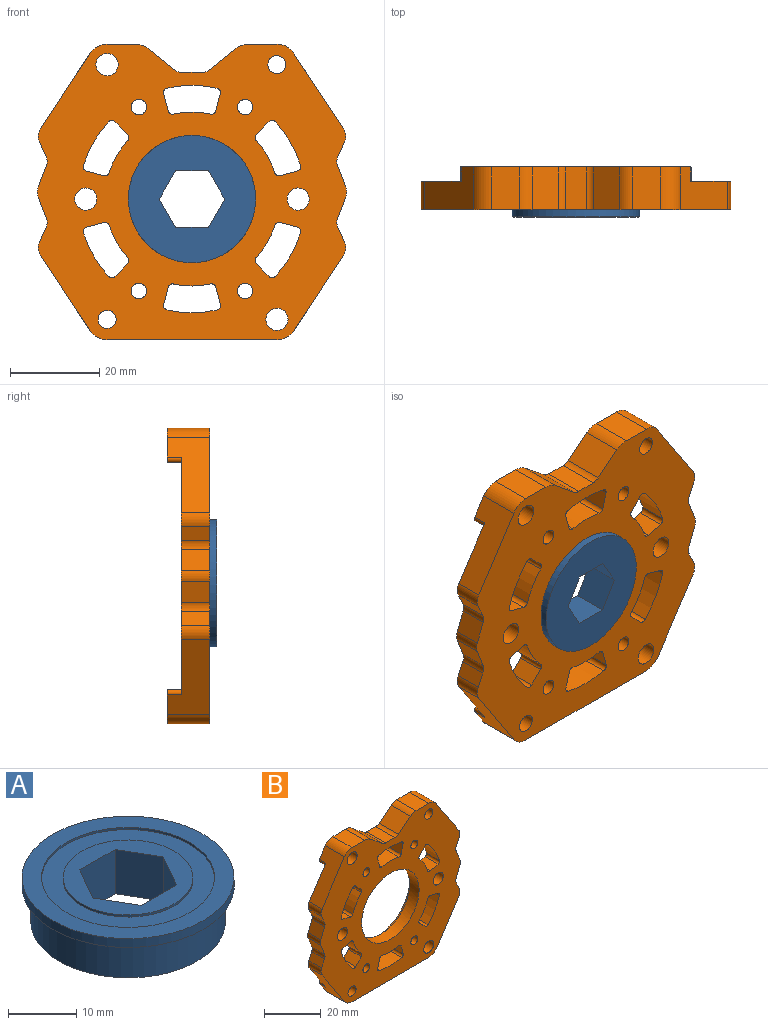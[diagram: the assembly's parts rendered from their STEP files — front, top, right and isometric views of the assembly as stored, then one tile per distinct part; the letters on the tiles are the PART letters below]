
ASSEMBLY  parts=2 mates=1
PART A: 15 faces, bbox 31.1x31.1x7.9 mm
  f0: cylinder r=12.7mm len=25.4mm, axis (0,0,1), area 30.4mm2, adj f7,f8
  f1: cylinder r=15.56mm len=31.12mm, axis (0,0,1), area 155.2mm2, adj f6,f7
  f2: cylinder r=14.27mm len=28.55mm, axis (0,0,1), area 569.5mm2, adj f5,f6
  f3: cylinder r=9.53mm len=19.05mm, axis (0,0,1), area 22.8mm2, adj f4,f8
  f4: plane 19.05x19.05mm, normal (0,0,1), area 144.9mm2, adj f3,f9,f10,f11,f12,f13,f14
  f5: plane 28.55x28.55mm, normal (0,0,-1), area 500mm2, adj f2,f9,f10,f11,f12,f13,f14
  f6: plane 31.12x31.12mm, normal (0,0,-1), area 120.2mm2, adj f1,f2
  f7: plane 31.12x31.12mm, normal (0,0,1), area 253.7mm2, adj f0,f1
  f8: plane 25.4x25.4mm, normal (0,0,1), area 221.7mm2, adj f0,f3
  f9: plane 7.94x6.36mm, normal (-0.87,-0.5,0), area 58.3mm2, adj f4,f5,f10,f14
  f10: plane 7.94x6.36mm, normal (-0.87,0.5,0), area 58.3mm2, adj f4,f5,f9,f11
  f11: plane 7.94x7.34mm, normal (0,1,0), area 58.3mm2, adj f4,f5,f10,f12
  f12: plane 7.94x6.36mm, normal (0.87,0.5,0), area 58.3mm2, adj f4,f5,f11,f13
  f13: plane 7.94x6.36mm, normal (0.87,-0.5,0), area 58.3mm2, adj f4,f5,f12,f14
  f14: plane 7.94x7.34mm, normal (0,-1,0), area 58.3mm2, adj f4,f5,f9,f13
PART B: 111 faces, bbox 69.4x9.5x66.3 mm
  f0: cylinder r=15.88mm len=31.75mm, axis (0,1,0), area 164.7mm2, adj f97,f110
  f1: cylinder r=2.54mm len=6.35mm, axis (0,-1,0), area 12.9mm2, adj f35,f36,f50,f97
  f2: cylinder r=2.54mm len=6.35mm, axis (0,1,0), area 12.9mm2, adj f44,f45,f50,f97
  f3: cylinder r=2.49mm len=6.35mm, axis (0,-1,0), area 99.3mm2, adj f50,f97
  f4: cylinder r=2.49mm len=6.35mm, axis (0,-1,0), area 99.3mm2, adj f50,f97
  f5: cylinder r=0.79mm len=3.18mm, axis (0,-1,0), area 5.3mm2, adj f25,f43,f96,f97,f102
  f6: cylinder r=0.79mm len=3.18mm, axis (0,1,0), area 5.3mm2, adj f25,f39,f95,f97,f101
  f7: cylinder r=2.02mm len=9.53mm, axis (0,-1,0), area 120.8mm2, adj f50,f51
  f8: cylinder r=2.02mm len=9.53mm, axis (0,-1,0), area 120.8mm2, adj f25,f50
  f9: cylinder r=3.17mm len=6.35mm, axis (0,1,0), area 14.8mm2, adj f36,f37,f50,f97
  f10: cylinder r=3.17mm len=6.35mm, axis (0,-1,0), area 20.5mm2, adj f47,f48,f50,f97
  f11: cylinder r=3.17mm len=6.35mm, axis (0,-1,0), area 20.4mm2, adj f43,f44,f50,f97
  f12: cylinder r=1mm len=6.35mm, axis (0,-1,0), area 9.7mm2, adj f50,f87,f93,f97
  f13: cylinder r=1mm len=9.53mm, axis (0,-1,0), area 14.5mm2, adj f25,f50,f82,f83,f96,f97,f102
  f14: cylinder r=1mm len=6.35mm, axis (0,-1,0), area 10.2mm2, adj f50,f73,f79,f97
  f15: cylinder r=1mm len=6.35mm, axis (0,-1,0), area 10.2mm2, adj f50,f66,f67,f97
  f16: cylinder r=1mm len=6.35mm, axis (0,-1,0), area 10.2mm2, adj f50,f59,f60,f97
  f17: cylinder r=1mm len=6.35mm, axis (0,-1,0), area 9.7mm2, adj f50,f52,f58,f97
  f18: cylinder r=1.73mm len=6.35mm, axis (0,-1,0), area 68.9mm2, adj f50,f97
  f19: cylinder r=1.73mm len=6.35mm, axis (0,-1,0), area 68.9mm2, adj f50,f97
  f20: cylinder r=1.73mm len=6.35mm, axis (0,-1,0), area 68.9mm2, adj f50,f97
  f21: cylinder r=1.73mm len=6.35mm, axis (0,-1,0), area 68.9mm2, adj f50,f97
  f22: cylinder r=2.49mm len=9.53mm, axis (0,1,0), area 149mm2, adj f50,f51
  f23: cylinder r=2.49mm len=9.53mm, axis (0,1,0), area 149mm2, adj f25,f50
  f24: cylinder r=14.27mm len=28.55mm, axis (0,1,0), area 421.5mm2, adj f50,f110
  f25: plane 51.79x7.45mm, normal (0,1,0), area 308.4mm2, adj f5,f6,f8,f13,f23,f39,f40,f41
  f26: plane 9.53x6.35mm, normal (0,0,1), area 60.5mm2, adj f27,f49,f50,f51
  f27: cylinder r=4.58mm len=9.53mm, axis (0,1,0), area 29.5mm2, adj f26,f28,f50,f51
  f28: plane 9.53x5.96mm, normal (-0.63,0,0.78), area 72.8mm2, adj f27,f50,f51,f106
  f29: plane 9.53x4.56mm, normal (0,0,1), area 43.5mm2, adj f50,f51,f106,f107
  f30: plane 9.53x5.96mm, normal (0.63,0,0.78), area 72.8mm2, adj f31,f50,f51,f107
  f31: cylinder r=4.58mm len=9.53mm, axis (0,1,0), area 29.5mm2, adj f30,f32,f50,f51
  f32: plane 9.53x6.35mm, normal (0,0,1), area 60.5mm2, adj f31,f33,f50,f51
  f33: cylinder r=4.58mm len=9.53mm, axis (0,1,0), area 43.3mm2, adj f32,f34,f50,f51
  f34: plane 16.91x11.08mm, normal (-0.84,0,0.55), area 145.1mm2, adj f33,f50,f51,f97,f99,f104
  f35: plane 6.35x3.19mm, normal (-0.91,0,-0.42), area 22.3mm2, adj f1,f50,f97,f99
  f36: plane 6.35x4.8mm, normal (-0.93,0,0.36), area 32.6mm2, adj f1,f9,f50,f97
  f37: plane 6.35x4.8mm, normal (-0.93,0,-0.36), area 32.6mm2, adj f9,f50,f97,f109
  f38: plane 6.35x3.19mm, normal (-0.91,0,0.42), area 22.3mm2, adj f50,f97,f98,f109
  f39: plane 16.91x11.08mm, normal (-0.84,0,-0.55), area 145.1mm2, adj f6,f25,f40,f50,f97,f98
  f40: cylinder r=4.58mm len=9.53mm, axis (0,1,0), area 43.3mm2, adj f25,f39,f41,f50
  f41: plane 38.1x9.53mm, normal (0,0,-1), area 362.9mm2, adj f25,f40,f42,f50
  f42: cylinder r=4.58mm len=9.53mm, axis (0,1,0), area 43.3mm2, adj f25,f41,f43,f50
  f43: plane 16.91x11.08mm, normal (0.84,0,-0.55), area 145.1mm2, adj f5,f11,f25,f42,f50,f97
  f44: plane 6.35x3.19mm, normal (0.91,0,0.42), area 22.3mm2, adj f2,f11,f50,f97
  f45: plane 6.35x4.8mm, normal (0.93,0,-0.36), area 32.6mm2, adj f2,f50,f97,f100
  f46: plane 6.35x4.8mm, normal (0.93,0,0.36), area 32.6mm2, adj f50,f97,f100,f108
  f47: plane 6.35x3.19mm, normal (0.91,0,-0.42), area 22.3mm2, adj f10,f50,f97,f108
  f48: plane 16.04x10.62mm, normal (0.83,0,0.55), area 135.6mm2, adj f10,f49,f50,f51,f97,f105
  f49: cylinder r=4.58mm len=9.53mm, axis (0,1,0), area 52.6mm2, adj f26,f48,f50,f51
  f50: plane 69.4x66.32mm, normal (0,-1,0), area 2716.2mm2, adj f1,f2,f3,f4,f7,f8,f9,f10
  f51: plane 51.69x7.45mm, normal (0,1,0), area 230.8mm2, adj f7,f22,f26,f27,f28,f29,f30,f31
  f52: cylinder r=19.5mm len=7.2mm, axis (0,-1,0), area 53.2mm2, adj f17,f50,f53,f97
  f53: cylinder r=1mm len=6.35mm, axis (0,-1,0), area 9.7mm2, adj f50,f52,f54,f97
  f54: plane 6.35x3.87mm, normal (0.26,0,0.97), area 25.4mm2, adj f50,f53,f55,f97
  f55: cylinder r=1mm len=6.35mm, axis (0,-1,0), area 10.2mm2, adj f50,f54,f56,f97
  f56: cylinder r=25.5mm len=9.75mm, axis (0,-1,0), area 72.1mm2, adj f50,f55,f57,f97
  f57: cylinder r=1mm len=6.35mm, axis (0,-1,0), area 10.2mm2, adj f50,f56,f58,f97
  f58: plane 6.35x2.83mm, normal (-0.71,0,-0.71), area 25.4mm2, adj f17,f50,f57,f97
  f59: cylinder r=25.5mm len=11.26mm, axis (0,-1,0), area 72.1mm2, adj f16,f50,f65,f97
  f60: plane 6.35x3.87mm, normal (-0.97,0,0.26), area 25.4mm2, adj f16,f50,f61,f97
  f61: cylinder r=1mm len=6.35mm, axis (0,-1,0), area 9.7mm2, adj f50,f60,f62,f97
  f62: cylinder r=19.5mm len=8.32mm, axis (0,-1,0), area 53.2mm2, adj f50,f61,f63,f97
  f63: cylinder r=1mm len=6.35mm, axis (0,-1,0), area 9.7mm2, adj f50,f62,f64,f97
  f64: plane 6.35x3.87mm, normal (0.97,0,0.26), area 25.4mm2, adj f50,f63,f65,f97
  f65: cylinder r=1mm len=6.35mm, axis (0,-1,0), area 10.2mm2, adj f50,f59,f64,f97
  f66: cylinder r=25.5mm len=9.74mm, axis (0,-1,0), area 72.1mm2, adj f15,f50,f72,f97
  f67: plane 6.35x3.87mm, normal (-0.26,0,0.97), area 25.4mm2, adj f15,f50,f68,f97
  f68: cylinder r=1mm len=6.35mm, axis (0,-1,0), area 9.7mm2, adj f50,f67,f69,f97
  f69: cylinder r=19.5mm len=7.2mm, axis (0,-1,0), area 53.2mm2, adj f50,f68,f70,f97
  f70: cylinder r=1mm len=6.35mm, axis (0,-1,0), area 9.7mm2, adj f50,f69,f71,f97
  f71: plane 6.35x2.83mm, normal (0.71,0,-0.71), area 25.4mm2, adj f50,f70,f72,f97
  f72: cylinder r=1mm len=6.35mm, axis (0,-1,0), area 10.2mm2, adj f50,f66,f71,f97
  f73: cylinder r=25.5mm len=9.75mm, axis (0,-1,0), area 72.1mm2, adj f14,f50,f74,f97
  f74: cylinder r=1mm len=6.35mm, axis (0,-1,0), area 10.2mm2, adj f50,f73,f75,f97
  f75: plane 6.35x2.83mm, normal (0.71,0,0.71), area 25.4mm2, adj f50,f74,f76,f97
  f76: cylinder r=1mm len=6.35mm, axis (0,-1,0), area 9.7mm2, adj f50,f75,f77,f97
  f77: cylinder r=19.5mm len=7.2mm, axis (0,-1,0), area 53.2mm2, adj f50,f76,f78,f97
  f78: cylinder r=1mm len=6.35mm, axis (0,-1,0), area 9.7mm2, adj f50,f77,f79,f97
  f79: plane 6.35x3.87mm, normal (-0.26,0,-0.97), area 25.4mm2, adj f14,f50,f78,f97
  f80: cylinder r=19.5mm len=8.32mm, axis (0,-1,0), area 53.2mm2, adj f50,f81,f86,f97
  f81: cylinder r=1mm len=6.35mm, axis (0,-1,0), area 9.7mm2, adj f50,f80,f82,f97
  f82: plane 6.35x3.87mm, normal (-0.97,0,-0.26), area 25.4mm2, adj f13,f50,f81,f97
  f83: cylinder r=25.5mm len=11.26mm, axis (0,-1,0), area 108.1mm2, adj f13,f25,f50,f84
  f84: cylinder r=1mm len=9.53mm, axis (0,-1,0), area 14.6mm2, adj f25,f50,f83,f85,f95,f97,f101
  f85: plane 6.35x3.87mm, normal (0.97,0,-0.26), area 25.4mm2, adj f50,f84,f86,f97
  f86: cylinder r=1mm len=6.35mm, axis (0,-1,0), area 9.7mm2, adj f50,f80,f85,f97
  f87: plane 6.35x2.83mm, normal (-0.71,0,0.71), area 25.4mm2, adj f12,f50,f88,f97
  f88: cylinder r=1mm len=6.35mm, axis (0,-1,0), area 10.2mm2, adj f50,f87,f89,f97
  f89: cylinder r=25.5mm len=9.74mm, axis (0,-1,0), area 72.1mm2, adj f50,f88,f90,f97
  f90: cylinder r=1mm len=6.35mm, axis (0,-1,0), area 10.2mm2, adj f50,f89,f91,f97
  f91: plane 6.35x3.87mm, normal (0.26,0,-0.97), area 25.4mm2, adj f50,f90,f92,f97
  f92: cylinder r=1mm len=6.35mm, axis (0,-1,0), area 9.7mm2, adj f50,f91,f93,f97
  f93: cylinder r=19.5mm len=7.2mm, axis (0,-1,0), area 53.2mm2, adj f12,f50,f92,f97
  f94: plane 50.1x2.93mm, normal (0,0,-1), area 146.5mm2, adj f97,f103,f104,f105
  f95: plane 18.7x2.93mm, normal (0,0,1), area 54.7mm2, adj f6,f84,f97,f101
  f96: plane 18.68x2.93mm, normal (0,0,1), area 54.6mm2, adj f5,f13,f97,f102
  f97: plane 69.4x53.39mm, normal (0,1,0), area 2003.2mm2, adj f0,f1,f2,f3,f4,f5,f6,f9
  f98: cylinder r=3.17mm len=6.35mm, axis (0,-1,0), area 20.4mm2, adj f38,f39,f50,f97
  f99: cylinder r=3.17mm len=6.35mm, axis (0,-1,0), area 20.4mm2, adj f34,f35,f50,f97
  f100: cylinder r=3.17mm len=6.35mm, axis (0,1,0), area 14.8mm2, adj f45,f46,f50,f97
  f101: plane 19.31x0.25mm, normal (0,0.71,0.71), area 6.8mm2, adj f6,f25,f84,f95
  f102: plane 19.29x0.25mm, normal (0,0.71,0.71), area 6.7mm2, adj f5,f13,f25,f96
  f103: plane 51.26x0.25mm, normal (0,0.71,-0.71), area 18mm2, adj f51,f94,f104,f105
  f104: cylinder r=0.79mm len=3.18mm, axis (0,-1,0), area 5.3mm2, adj f34,f51,f94,f97,f103
  f105: cylinder r=0.79mm len=3.18mm, axis (0,1,0), area 5.3mm2, adj f48,f51,f94,f97,f103
  f106: cylinder r=2.54mm len=9.53mm, axis (0,-1,0), area 16.4mm2, adj f28,f29,f50,f51
  f107: cylinder r=2.54mm len=9.53mm, axis (0,-1,0), area 16.4mm2, adj f29,f30,f50,f51
  f108: cylinder r=2.54mm len=6.35mm, axis (0,-1,0), area 12.9mm2, adj f46,f47,f50,f97
  f109: cylinder r=2.54mm len=6.35mm, axis (0,1,0), area 12.9mm2, adj f37,f38,f50,f97
  f110: plane 31.75x31.75mm, normal (0,1,0), area 151.6mm2, adj f0,f24
PLACE A rot(axis=(-1,0,0),90deg) t=(0,-6.41,-1.59)mm
PLACE B at identity fixed
MATE revolute B.f0 <-> A.f0  axis (0,1,0) through (0,-0.06,-1.59)mm
